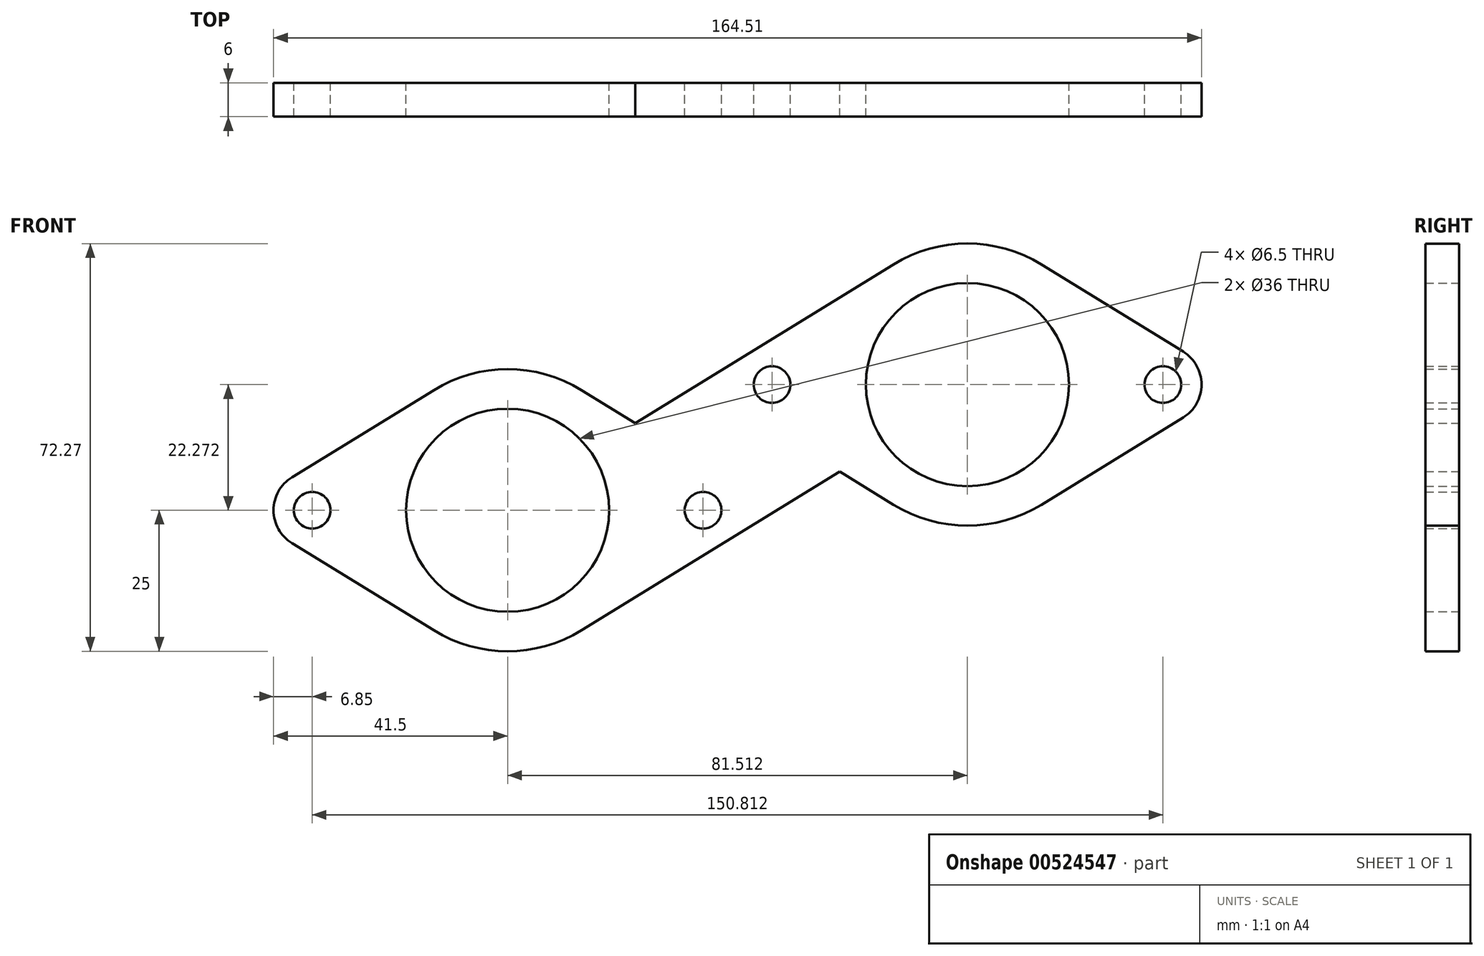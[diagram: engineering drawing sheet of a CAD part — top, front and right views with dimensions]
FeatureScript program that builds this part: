
annotation { "Feature Type Name" : "Feature", "Feature Type Description" : "" }
export const myFeature = defineFeature(function(context is Context, id is Id, definition is map)
    precondition{}
    {
        {
            var Q0;
            Q0=qCreatedBy(makeId("Front.planeOp"),FACE);
            var sketch = newSketch(context, id + "F0", { "sketchPlane" : qUnion([Q0])});
            skCircle(sketch, "E0", {"center": v(0, 0) * mm, "radius": 18 * mm});
            skCircle(sketch, "E1", {"center": v(0, 0) * mm, "radius": 34.65 * mm, "construction": true});
            skCircle(sketch, "E2", {"center": v(-34.65, 0) * mm, "radius": 3.25 * mm});
            skCircle(sketch, "E3", {"center": v(34.65, 0) * mm, "radius": 3.25 * mm});
            skArc(sketch, "E4", {"start": v(-13.1, -21.3) * mm, "mid": v(0, -25) * mm, "end": v(13.1, -21.3) * mm});
            skCircle(sketch, "E5", {"center": v(0, 0) * mm, "radius": 41.5 * mm, "construction": true});
            skArc(sketch, "E6", {"start": v(-38.24, 5.84) * mm, "mid": v(-41.5, 0) * mm, "end": v(-38.24, -5.84) * mm});
            skLineSegment(sketch, "E7", {"start": v(-13.1, 21.3) * mm, "end": v(-38.24, 5.84) * mm});
            skLineSegment(sketch, "E8", {"start": v(-38.24, -5.84) * mm, "end": v(-13.1, -21.3) * mm});
            skLineSegment(sketch, "E9", {"start": v(13.1, 21.3) * mm, "end": v(22.65, 15.42) * mm});
            skLineSegment(sketch, "E10", {"start": v(13.1, -21.3) * mm, "end": v(58.87, 6.85) * mm});
            skArc(sketch, "E11.trimOffspring", {"start": v(13.1, 21.3) * mm, "mid": v(0, 25) * mm, "end": v(-13.1, 21.3) * mm});
            skCircle(sketch, "E12", {"center": v(34.65, 0) * mm, "radius": 25.4 * mm, "construction": true});
            skLineSegment(sketch, "E13.trimOffspring", {"start": v(58.87, 6.85) * mm, "end": v(68.42, 0.98) * mm});
            skLineSegment(sketch, "E14", {"start": v(46.86, 22.27) * mm, "end": v(119.9, 22.27) * mm, "construction": true});
            skArc(sketch, "E15", {"start": v(68.42, 0.98) * mm, "mid": v(81.51, -2.73) * mm, "end": v(94.6, 0.98) * mm});
            skCircle(sketch, "E16", {"center": v(81.51, 22.27) * mm, "radius": 18 * mm});
            skCircle(sketch, "E17", {"center": v(81.51, 22.27) * mm, "radius": 34.65 * mm, "construction": true});
            skArc(sketch, "E18", {"start": v(119.75, 16.44) * mm, "mid": v(123.01, 22.27) * mm, "end": v(119.75, 28.1) * mm});
            skCircle(sketch, "E19", {"center": v(116.16, 22.27) * mm, "radius": 3.25 * mm});
            skCircle(sketch, "E20", {"center": v(46.86, 22.27) * mm, "radius": 3.25 * mm});
            skLineSegment(sketch, "E21", {"start": v(94.6, 43.57) * mm, "end": v(119.75, 28.1) * mm});
            skLineSegment(sketch, "E22", {"start": v(94.6, 0.98) * mm, "end": v(119.75, 16.44) * mm});
            skLineSegment(sketch, "E23", {"start": v(68.42, 43.57) * mm, "end": v(22.65, 15.42) * mm});
            skArc(sketch, "E24.trimOffspring", {"start": v(94.6, 43.57) * mm, "mid": v(81.51, 47.27) * mm, "end": v(68.42, 43.57) * mm});
            skSolve(sketch);
        }
        {
            var Q0;
            Q0=makeQuery(id+"F0.imprint","IMPRINT",FACE,{"disambiguationData":[TD([[makeQuery(id+"F0.imprint","IMPRINT",EDGE,{"derivedFrom":sQuery(id+"F0.wireOp",EDGE,"E0")}),-1.0]])]});
            extrude(context, id + "F1", {"entities" : qUnion([Q0]), "depth" : 6 * mm, "offsetDistance" : 25 * mm});
        }
    });
